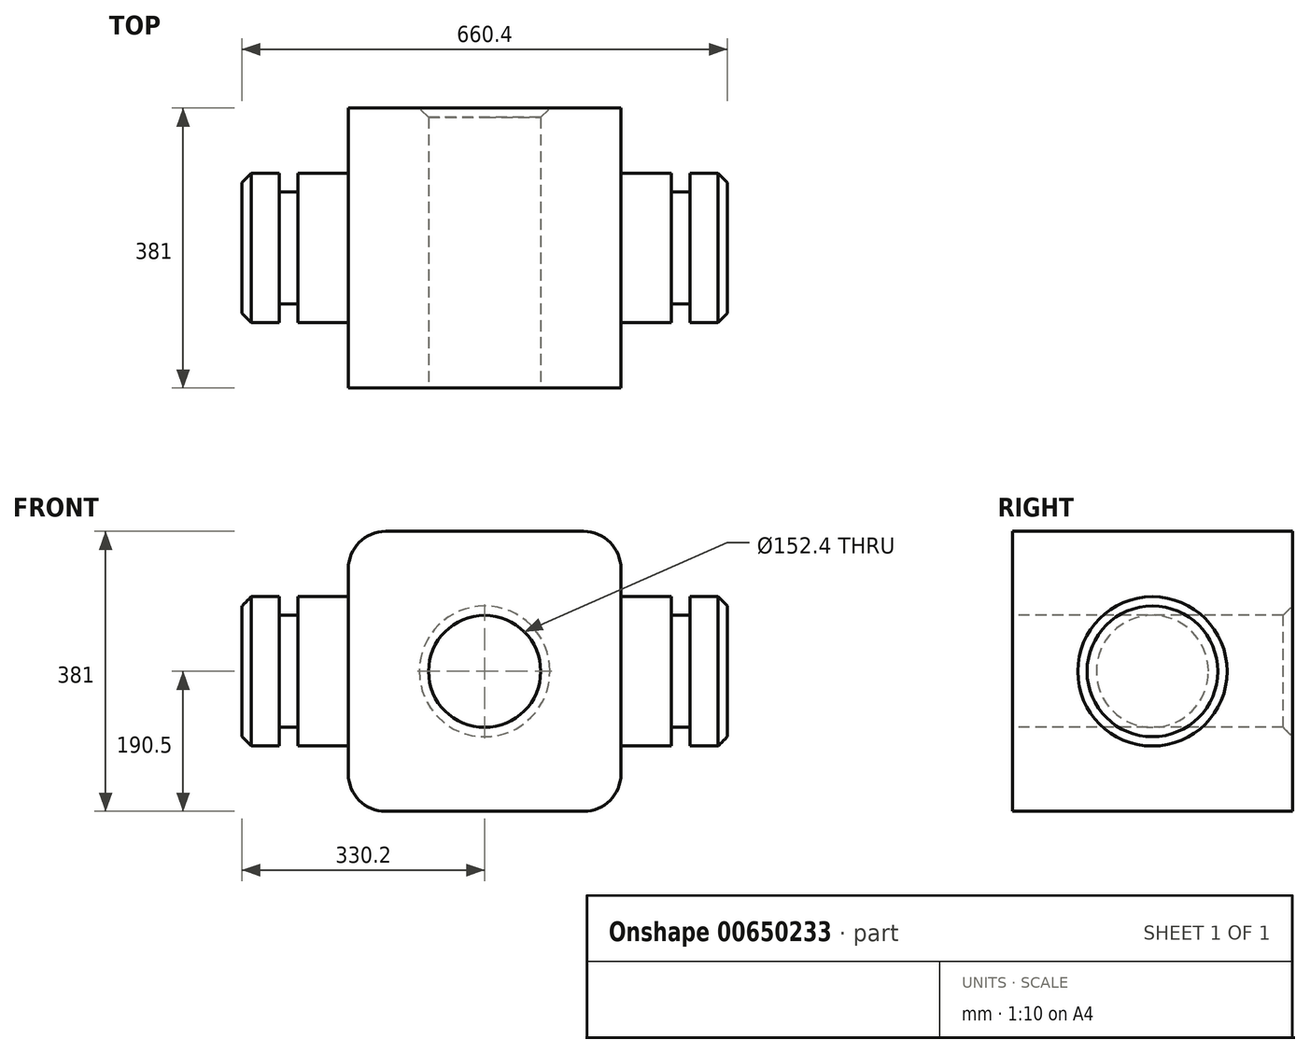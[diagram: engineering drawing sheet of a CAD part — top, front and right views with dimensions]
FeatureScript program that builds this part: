
annotation { "Feature Type Name" : "Feature", "Feature Type Description" : "" }
export const myFeature = defineFeature(function(context is Context, id is Id, definition is map)
    precondition{}
    {
        {
            var Q0;
            Q0=qCreatedBy(makeId("Front.planeOp"),FACE);
            var sketch = newSketch(context, id + "F0", { "sketchPlane" : qUnion([Q0])});
            skLineSegment(sketch, "E0", {"start": v(-72.3, 0) * mm, "end": v(66.81, 0) * mm, "construction": true});
            skLineSegment(sketch, "E1", {"start": v(0, 67.25) * mm, "end": v(0, -69.73) * mm, "construction": true});
            skSolve(sketch);
        }
        {
            var Q0;
            Q0=qCreatedBy(makeId("Front.planeOp"),FACE);
            var sketch = newSketch(context, id + "F1", { "sketchPlane" : qUnion([Q0])});
            skLineSegment(sketch, "E2.bottom", {"start": v(-134.62, -190.5) * mm, "end": v(134.62, -190.5) * mm});
            skLineSegment(sketch, "E2.top", {"start": v(-134.62, 190.5) * mm, "end": v(134.62, 190.5) * mm});
            skLineSegment(sketch, "E2.left", {"start": v(-185.42, -139.7) * mm, "end": v(-185.42, 139.7) * mm});
            skLineSegment(sketch, "E2.right", {"start": v(185.42, -139.7) * mm, "end": v(185.42, 139.7) * mm});
            skPoint(sketch, "E2.middle", {"position": v(0, 0) * mm});
            skPoint(sketch, "E3.visualSharp", {"position": v(-185.42, 190.5) * mm});
            skArc(sketch, "E3.filletArc", {"start": v(-134.62, 190.5) * mm, "mid": v(-170.54, 175.62) * mm, "end": v(-185.42, 139.7) * mm});
            skPoint(sketch, "E4.visualSharp", {"position": v(-185.42, -190.5) * mm});
            skArc(sketch, "E4.filletArc", {"start": v(-185.42, -139.7) * mm, "mid": v(-170.54, -175.62) * mm, "end": v(-134.62, -190.5) * mm});
            skPoint(sketch, "E5.visualSharp", {"position": v(185.42, 190.5) * mm});
            skArc(sketch, "E5.filletArc", {"start": v(185.42, 139.7) * mm, "mid": v(170.54, 175.62) * mm, "end": v(134.62, 190.5) * mm});
            skPoint(sketch, "E6.visualSharp", {"position": v(185.42, -190.5) * mm});
            skArc(sketch, "E6.filletArc", {"start": v(134.62, -190.5) * mm, "mid": v(170.54, -175.62) * mm, "end": v(185.42, -139.7) * mm});
            skSolve(sketch);
        }
        {
            var Q0;
            Q0=makeQuery(id+"F1.imprint","IMPRINT",FACE,{"disambiguationData":[TD([[makeQuery(id+"F1.imprint","IMPRINT",EDGE,{"derivedFrom":sQuery(id+"F1.wireOp",EDGE,"E2.bottom")}),1.0]])]});
            extrude(context, id + "F2", {"entities" : qUnion([Q0]), "depth" : 381 * mm, "offsetDistance" : 25.4 * mm});
        }
        {
            var Q0;
            Q0=makeQuery(id+"F2.opExtrude","SWEPT_FACE",FACE,{"disambiguationData":[OSD([sQuery(id+"F1.wireOp",EDGE,"E2.right")])]});
            var sketch = newSketch(context, id + "F3", { "sketchPlane" : qUnion([Q0])});
            skCircle(sketch, "E7", {"center": v(-190.5, 0) * mm, "radius": 101.6 * mm});
            skSolve(sketch);
        }
        {
            var Q0;
            Q0=makeQuery(id+"F3.imprint","IMPRINT",FACE,{"disambiguationData":[TD([[makeQuery(id+"F3.imprint","IMPRINT",EDGE,{"derivedFrom":sQuery(id+"F3.wireOp",EDGE,"E7")}),1.0]])]});
            extrude(context, id + "F4", {"entities" : qUnion([Q0]), "operationType" : NewBodyOperationType.ADD, "depth" : 68.58 * mm, "offsetDistance" : 25.4 * mm});
        }
        {
            var Q0;
            Q0=makeQuery(id+"F2.opExtrude","SWEPT_FACE",FACE,{"disambiguationData":[OSD([sQuery(id+"F1.wireOp",EDGE,"E2.left")])]});
            var sketch = newSketch(context, id + "F5", { "sketchPlane" : qUnion([Q0])});
            skCircle(sketch, "E8", {"center": v(190.5, 0) * mm, "radius": 101.6 * mm});
            skSolve(sketch);
        }
        {
            var Q0;
            Q0=makeQuery(id+"F5.imprint","IMPRINT",FACE,{"disambiguationData":[TD([[makeQuery(id+"F5.imprint","IMPRINT",EDGE,{"derivedFrom":sQuery(id+"F5.wireOp",EDGE,"E8")}),1.0]])]});
            extrude(context, id + "F6", {"entities" : qUnion([Q0]), "operationType" : NewBodyOperationType.ADD, "depth" : 68.58 * mm, "offsetDistance" : 25.4 * mm});
        }
        {
            var Q0;
            Q0=makeQuery(id+"F2.opExtrude","CAP_FACE",FACE,{"disambiguationData":[OSD([sQuery(id+"F1.wireOp",EDGE,"E2.bottom"),sQuery(id+"F1.wireOp",EDGE,"E2.top"),sQuery(id+"F1.wireOp",EDGE,"E2.left"),sQuery(id+"F1.wireOp",EDGE,"E2.right"),sQuery(id+"F1.wireOp",EDGE,"E3.filletArc"),sQuery(id+"F1.wireOp",EDGE,"E4.filletArc"),sQuery(id+"F1.wireOp",EDGE,"E5.filletArc"),sQuery(id+"F1.wireOp",EDGE,"E6.filletArc")])],"isStart":false});
            var sketch = newSketch(context, id + "F7", { "sketchPlane" : qUnion([Q0])});
            skCircle(sketch, "E9", {"center": v(0, 0) * mm, "radius": 76.2 * mm});
            skSolve(sketch);
        }
        {
            var Q0;
            Q0=makeQuery(id+"F7.imprint","IMPRINT",FACE,{"disambiguationData":[TD([[makeQuery(id+"F7.imprint","IMPRINT",EDGE,{"derivedFrom":sQuery(id+"F7.wireOp",EDGE,"E9")}),1.0]])]});
            extrude(context, id + "F8", {"entities" : qUnion([Q0]), "operationType" : NewBodyOperationType.REMOVE, "oppositeDirection" : true, "depth" : 508 * mm, "offsetDistance" : 25.4 * mm});
        }
        {
            var Q0;
            Q0=makeQuery(id+"F8.boolean.opBoolean","COPY",EDGE,{"derivedFrom":makeQuery(id+"F8.opExtrude","CAP_EDGE",EDGE,{"disambiguationData":[OSD([sQuery(id+"F7.wireOp",EDGE,"E9")])],"isStart":true})});
            var Q1;
            Q1=makeQuery(id+"F8.boolean.opBoolean","INTERSECT",EDGE,{"derivedFrom":[makeQuery(id+"F2.opExtrude","CAP_FACE",FACE,{"disambiguationData":[OSD([sQuery(id+"F1.wireOp",EDGE,"E2.bottom"),sQuery(id+"F1.wireOp",EDGE,"E2.top"),sQuery(id+"F1.wireOp",EDGE,"E2.left"),sQuery(id+"F1.wireOp",EDGE,"E2.right"),sQuery(id+"F1.wireOp",EDGE,"E3.filletArc"),sQuery(id+"F1.wireOp",EDGE,"E4.filletArc"),sQuery(id+"F1.wireOp",EDGE,"E5.filletArc"),sQuery(id+"F1.wireOp",EDGE,"E6.filletArc")])],"isStart":true}),makeQuery(id+"F8.opExtrude","SWEPT_FACE",FACE,{"disambiguationData":[OSD([sQuery(id+"F7.wireOp",EDGE,"E9")])]})]});
            chamfer(context, id + "F9", {"entities" : qUnion([Q0, Q1]), "chamferType" : ChamferType.OFFSET_ANGLE, "width" : 12.7 * mm, "oppositeDirection" : false, "angle" : 45 * degree, "tangentPropagation" : true});
        }
        {
            var Q0;
            Q0=makeQuery(id+"F6.opExtrude","CAP_FACE",FACE,{"disambiguationData":[OSD([sQuery(id+"F5.wireOp",EDGE,"E8")])],"isStart":false});
            var sketch = newSketch(context, id + "F10", { "sketchPlane" : qUnion([Q0])});
            skCircle(sketch, "E10", {"center": v(190.5, 0) * mm, "radius": 76.2 * mm});
            skSolve(sketch);
        }
        {
            var Q0;
            Q0=makeQuery(id+"F4.opExtrude","CAP_FACE",FACE,{"disambiguationData":[OSD([sQuery(id+"F3.wireOp",EDGE,"E7")])],"isStart":false});
            var sketch = newSketch(context, id + "F11", { "sketchPlane" : qUnion([Q0])});
            skCircle(sketch, "E11", {"center": v(-190.5, 0) * mm, "radius": 76.2 * mm});
            skSolve(sketch);
        }
        {
            var Q0;
            Q0=makeQuery(id+"F11.imprint","IMPRINT",FACE,{"disambiguationData":[TD([[makeQuery(id+"F11.imprint","IMPRINT",EDGE,{"derivedFrom":sQuery(id+"F11.wireOp",EDGE,"E11")}),1.0]])]});
            extrude(context, id + "F12", {"entities" : qUnion([Q0]), "operationType" : NewBodyOperationType.ADD, "depth" : 25.4 * mm, "offsetDistance" : 25.4 * mm});
        }
        {
            var Q0;
            Q0=makeQuery(id+"F10.imprint","IMPRINT",FACE,{"disambiguationData":[TD([[makeQuery(id+"F10.imprint","IMPRINT",EDGE,{"derivedFrom":sQuery(id+"F10.wireOp",EDGE,"E10")}),1.0]])]});
            extrude(context, id + "F13", {"entities" : qUnion([Q0]), "operationType" : NewBodyOperationType.ADD, "depth" : 25.4 * mm, "offsetDistance" : 25.4 * mm});
        }
        {
            var Q0;
            Q0=makeQuery(id+"F12.opExtrude","CAP_FACE",FACE,{"disambiguationData":[OSD([sQuery(id+"F11.wireOp",EDGE,"E11")])],"isStart":false});
            var sketch = newSketch(context, id + "F14", { "sketchPlane" : qUnion([Q0])});
            skCircle(sketch, "E12", {"center": v(-190.5, 0) * mm, "radius": 101.6 * mm});
            skSolve(sketch);
        }
        {
            var Q0;
            Q0=makeQuery(id+"F14.imprint","IMPRINT",FACE,{"disambiguationData":[TD([[makeQuery(id+"F14.imprint","IMPRINT",EDGE,{"derivedFrom":sQuery(id+"F14.wireOp",EDGE,"E12")}),1.0]])]});
            var Q1;
            Q1 = qSketchRegion(id + "F14", true);
            var Q2;
            Q2=makeQuery(id+"F14.imprint","IMPRINT",FACE,{"disambiguationData":[TD([[makeQuery(id+"F14.imprint","IMPRINT",EDGE,{"derivedFrom":makeQuery(id+"F12.opExtrude","CAP_EDGE",EDGE,{"disambiguationData":[OSD([sQuery(id+"F11.wireOp",EDGE,"E11")])],"isStart":false})}),1.0]])]});
            extrude(context, id + "F15", {"entities" : qUnion([Q0, Q1, Q2]), "operationType" : NewBodyOperationType.ADD, "depth" : 50.8 * mm, "offsetDistance" : 25.4 * mm});
        }
        {
            var Q0;
            Q0=makeQuery(id+"F13.opExtrude","CAP_FACE",FACE,{"disambiguationData":[OSD([sQuery(id+"F10.wireOp",EDGE,"E10")])],"isStart":false});
            var sketch = newSketch(context, id + "F16", { "sketchPlane" : qUnion([Q0])});
            skCircle(sketch, "E13", {"center": v(190.5, 0) * mm, "radius": 101.6 * mm});
            skSolve(sketch);
        }
        {
            var Q0;
            Q0 = qSketchRegion(id + "F16", true);
            extrude(context, id + "F17", {"entities" : qUnion([Q0]), "operationType" : NewBodyOperationType.ADD, "depth" : 50.8 * mm, "offsetDistance" : 25.4 * mm});
        }
        {
            var Q0;
            Q0=makeQuery(id+"F15.opExtrude","CAP_EDGE",EDGE,{"disambiguationData":[OSD([sQuery(id+"F14.wireOp",EDGE,"E12")])],"isStart":false});
            var Q1;
            Q1=makeQuery(id+"F17.opExtrude","CAP_EDGE",EDGE,{"disambiguationData":[OSD([sQuery(id+"F16.wireOp",EDGE,"E13")])],"isStart":false});
            chamfer(context, id + "F18", {"entities" : qUnion([Q0, Q1]), "chamferType" : ChamferType.OFFSET_ANGLE, "width" : 12.7 * mm, "oppositeDirection" : false, "angle" : 45 * degree, "tangentPropagation" : true});
        }
    });
